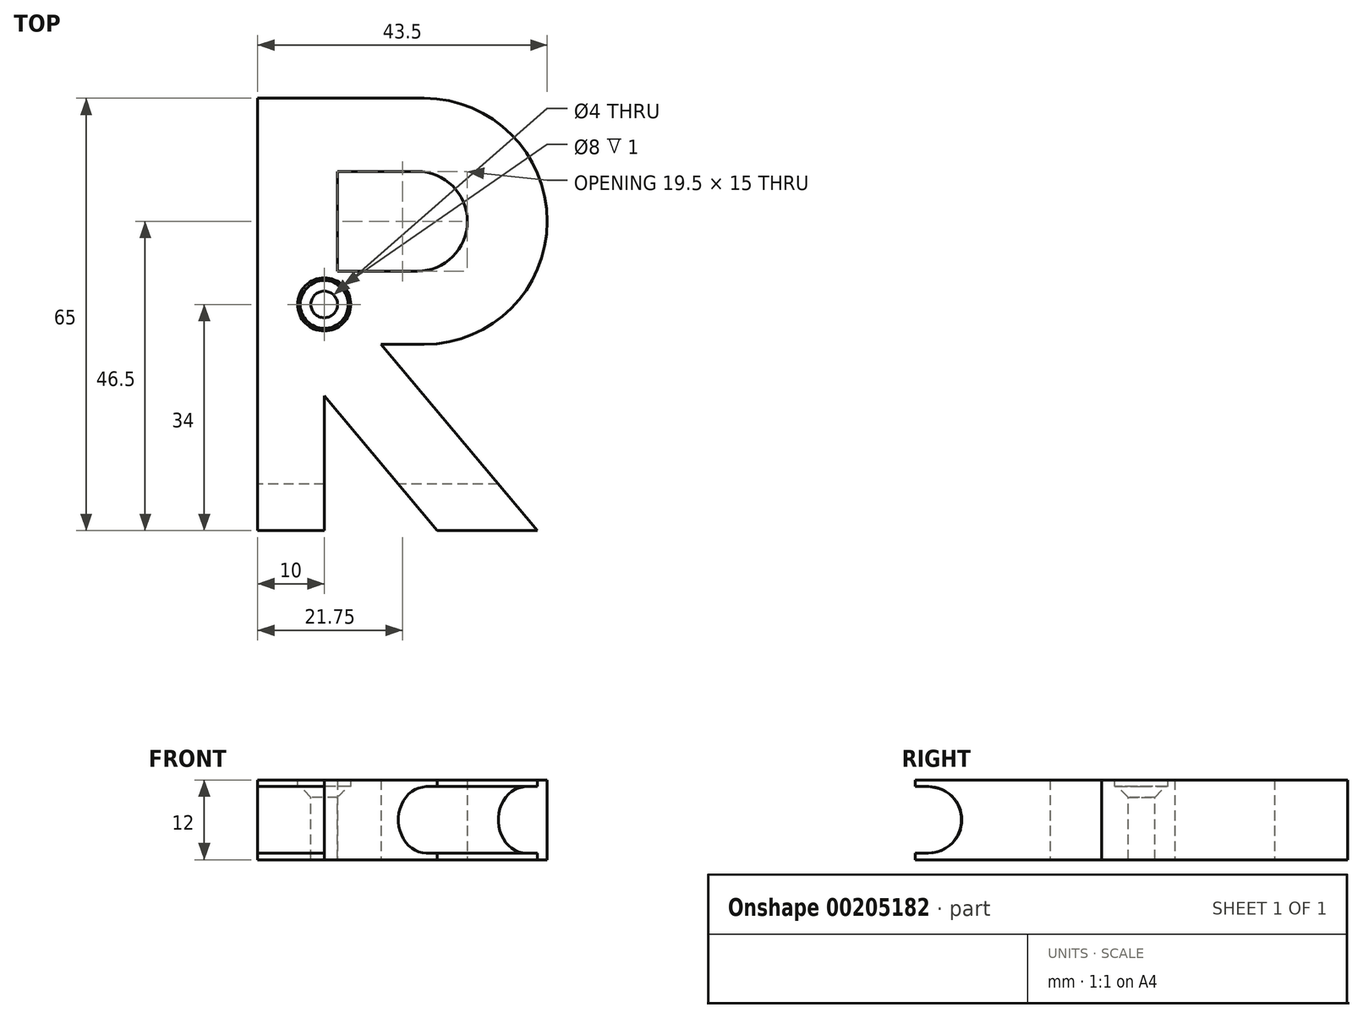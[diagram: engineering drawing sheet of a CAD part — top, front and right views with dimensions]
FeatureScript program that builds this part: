
annotation { "Feature Type Name" : "Feature", "Feature Type Description" : "" }
export const myFeature = defineFeature(function(context is Context, id is Id, definition is map)
    precondition{}
    {
        {
            var Q0;
            Q0=qCreatedBy(makeId("Top.planeOp"),FACE);
            var sketch = newSketch(context, id + "F0", { "sketchPlane" : qUnion([Q0])});
            skLineSegment(sketch, "E0", {"start": v(-30, 32.5) * mm, "end": v(-30, -32.5) * mm});
            skLineSegment(sketch, "E1", {"start": v(-30, 32.5) * mm, "end": v(-5, 32.5) * mm});
            skLineSegment(sketch, "E2", {"start": v(-5, 32.5) * mm, "end": v(-5, -4.5) * mm, "construction": true});
            skArc(sketch, "E3", {"start": v(-5, -4.5) * mm, "mid": v(13.5, 14) * mm, "end": v(-5, 32.5) * mm});
            skLineSegment(sketch, "E4", {"start": v(-30, -32.5) * mm, "end": v(-20, -32.5) * mm});
            skLineSegment(sketch, "E5", {"start": v(-20, -32.5) * mm, "end": v(-20, -12.24) * mm});
            skLineSegment(sketch, "E6", {"start": v(-20, -12.24) * mm, "end": v(-3, -32.5) * mm});
            skLineSegment(sketch, "E7", {"start": v(-11.5, -4.5) * mm, "end": v(-5, -4.5) * mm});
            skLineSegment(sketch, "E8", {"start": v(-3, -32.5) * mm, "end": v(12, -32.5) * mm});
            skLineSegment(sketch, "E9", {"start": v(12, -32.5) * mm, "end": v(-11.5, -4.5) * mm});
            skLineSegment(sketch, "E10.bottom", {"start": v(-18, 21.5) * mm, "end": v(-6, 21.5) * mm});
            skLineSegment(sketch, "E10.top", {"start": v(-18, 6.5) * mm, "end": v(-6, 6.5) * mm});
            skLineSegment(sketch, "E10.left", {"start": v(-18, 21.5) * mm, "end": v(-18, 6.5) * mm});
            skLineSegment(sketch, "E10.right", {"start": v(-6, 21.5) * mm, "end": v(-6, 6.5) * mm, "construction": true});
            skArc(sketch, "E11", {"start": v(-6, 6.5) * mm, "mid": v(1.5, 14) * mm, "end": v(-6, 21.5) * mm});
            skSolve(sketch);
        }
        {
            var Q0;
            Q0=makeQuery(id+"F0.imprint","IMPRINT",FACE,{"disambiguationData":[TD([[makeQuery(id+"F0.imprint","IMPRINT",EDGE,{"derivedFrom":sQuery(id+"F0.wireOp",EDGE,"E0")}),1.0]])]});
            var Q1;
            Q1=sQuery(id+"F0.wireOp",EDGE,"E10.right");
            extrude(context, id + "F1", {"entities" : qUnion([Q0]), "surfaceEntities" : qUnion([Q1]), "depth" : 12 * mm});
        }
        {
            var Q0;
            Q0=makeQuery(id+"F1.opExtrude","SWEPT_FACE",FACE,{"disambiguationData":[OSD([sQuery(id+"F0.wireOp",EDGE,"E0")])]});
            var sketch = newSketch(context, id + "F2", { "sketchPlane" : qUnion([Q0])});
            skLineSegment(sketch, "E12", {"start": v(32.5, 6) * mm, "end": v(30.5, 6) * mm, "construction": true});
            skArc(sketch, "E13", {"start": v(30.5, 11) * mm, "mid": v(25.5, 6) * mm, "end": v(30.5, 1) * mm});
            skLineSegment(sketch, "E14", {"start": v(30.5, 11) * mm, "end": v(32.5, 11) * mm});
            skLineSegment(sketch, "E15", {"start": v(30.5, 1) * mm, "end": v(32.5, 1) * mm});
            skLineSegment(sketch, "E16", {"start": v(32.5, 1) * mm, "end": v(32.5, 11) * mm});
            skSolve(sketch);
        }
        {
            var Q0;
            Q0 = qSketchRegion(id + "F2", true);
            extrude(context, id + "F3", {"entities" : qUnion([Q0]), "operationType" : NewBodyOperationType.REMOVE, "endBound" : BoundingType.THROUGH_ALL, "oppositeDirection" : true, "depth" : 25 * mm});
        }
        {
            var Q0;
            Q0=makeQuery(id+"F1.opExtrude","CAP_FACE",FACE,{"disambiguationData":[OSD([sQuery(id+"F0.wireOp",EDGE,"E0"),sQuery(id+"F0.wireOp",EDGE,"E1"),sQuery(id+"F0.wireOp",EDGE,"E3"),sQuery(id+"F0.wireOp",EDGE,"E4"),sQuery(id+"F0.wireOp",EDGE,"E5"),sQuery(id+"F0.wireOp",EDGE,"E6"),sQuery(id+"F0.wireOp",EDGE,"E7"),sQuery(id+"F0.wireOp",EDGE,"E8"),sQuery(id+"F0.wireOp",EDGE,"E9"),sQuery(id+"F0.wireOp",EDGE,"E10.bottom"),sQuery(id+"F0.wireOp",EDGE,"E10.top"),sQuery(id+"F0.wireOp",EDGE,"E10.left"),sQuery(id+"F0.wireOp",EDGE,"E11")])],"isStart":false});
            var sketch = newSketch(context, id + "F4", { "sketchPlane" : qUnion([Q0])});
            skCircle(sketch, "E17", {"center": v(-20, 1.5) * mm, "radius": 2 * mm});
            skSolve(sketch);
        }
        {
            var Q0;
            Q0 = qSketchRegion(id + "F4", true);
            extrude(context, id + "F5", {"entities" : qUnion([Q0]), "operationType" : NewBodyOperationType.REMOVE, "endBound" : BoundingType.THROUGH_ALL, "oppositeDirection" : true, "depth" : 25 * mm});
        }
        {
            var Q0;
            Q0=makeQuery(id+"F1.opExtrude","CAP_FACE",FACE,{"disambiguationData":[OSD([sQuery(id+"F0.wireOp",EDGE,"E0"),sQuery(id+"F0.wireOp",EDGE,"E1"),sQuery(id+"F0.wireOp",EDGE,"E3"),sQuery(id+"F0.wireOp",EDGE,"E4"),sQuery(id+"F0.wireOp",EDGE,"E5"),sQuery(id+"F0.wireOp",EDGE,"E6"),sQuery(id+"F0.wireOp",EDGE,"E7"),sQuery(id+"F0.wireOp",EDGE,"E8"),sQuery(id+"F0.wireOp",EDGE,"E9"),sQuery(id+"F0.wireOp",EDGE,"E10.bottom"),sQuery(id+"F0.wireOp",EDGE,"E10.top"),sQuery(id+"F0.wireOp",EDGE,"E10.left"),sQuery(id+"F0.wireOp",EDGE,"E11")])],"isStart":false});
            var sketch = newSketch(context, id + "F6", { "sketchPlane" : qUnion([Q0])});
            skCircle(sketch, "E18", {"center": v(-20, 1.5) * mm, "radius": 4 * mm});
            skSolve(sketch);
        }
        {
            var Q0;
            Q0 = qSketchRegion(id + "F6", true);
            extrude(context, id + "F7", {"entities" : qUnion([Q0]), "operationType" : NewBodyOperationType.REMOVE, "oppositeDirection" : true, "depth" : 1 * mm});
        }
        {
            var Q0;
            Q0=makeQuery(id+"F7.boolean.opBoolean","INTERSECT",EDGE,{"derivedFrom":[makeQuery(id+"F5.boolean.opBoolean","COPY",FACE,{"derivedFrom":makeQuery(id+"F5.opExtrude","SWEPT_FACE",FACE,{"disambiguationData":[OSD([sQuery(id+"F4.wireOp",EDGE,"E17")])]})}),makeQuery(id+"F7.opExtrude","CAP_FACE",FACE,{"disambiguationData":[OSD([sQuery(id+"F6.wireOp",EDGE,"E18")])],"isStart":false})]});
            chamfer(context, id + "F8", {"entities" : qUnion([Q0]), "width" : 1.6 * mm, "tangentPropagation" : true});
        }
    });
